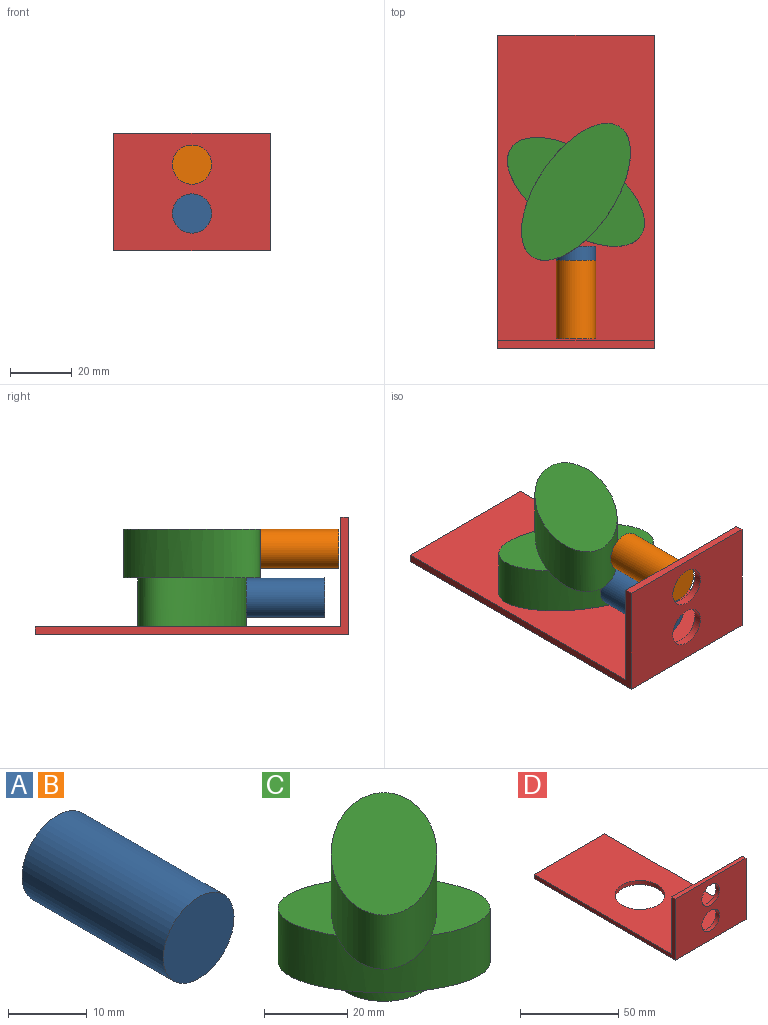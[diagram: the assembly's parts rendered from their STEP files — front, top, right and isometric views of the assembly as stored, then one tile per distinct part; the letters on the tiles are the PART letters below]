
ASSEMBLY  parts=4 mates=3
PART A: 3 faces, bbox 12.7x25.4x12.7 mm
  f0: cylinder r=6.35mm len=25.4mm, axis (0,1,0), area 1013.4mm2, adj f1,f2
  f1: plane 12.7x12.7mm, normal (0,-1,0), area 126.7mm2, adj f0
  f2: plane 12.7x12.7mm, normal (0,1,0), area 126.7mm2, adj f0
PART B: same geometry as A
PART C: 11 faces, bbox 40.2x40.2x34.3 mm
  f0: plane 29.06x29.06mm, normal (0,0,-1), area 253.4mm2, adj f2,f9
  f1: plane 20.08x20.08mm, normal (0,0,1), area 207.6mm2, adj f2,f7
  f2: extruded ~40.16x40.1mm, area 1953.4mm2, adj f0,f1,f3,f4,f5,f6
  f3: plane 20.08x20.08mm, normal (0,0,1), area 207.6mm2, adj f2,f7
  f4: plane 29.06x29.06mm, normal (0,0,-1), area 253.4mm2, adj f2,f9
  f5: plane 20.08x20.08mm, normal (0,0,-1), area 207.6mm2, adj f2,f7
  f6: plane 20.08x20.08mm, normal (0,0,-1), area 207.6mm2, adj f2,f7
  f7: extruded ~40.06x40.06mm, area 1953.4mm2, adj f1,f3,f5,f6,f8
  f8: plane 40.16x40.16mm, normal (0,0,1), area 1013.4mm2, adj f7
  f9: cylinder r=12.7mm len=25.4mm, axis (0,0,1), area 202.7mm2, adj f0,f4,f10
  f10: plane 25.4x25.4mm, normal (0,0,-1), area 506.7mm2, adj f9
PART D: 11 faces, bbox 50.8x101.6x38.1 mm
  f0: plane 99.06x50.8mm, normal (0,0,1), area 4525.5mm2, adj f1,f2,f3,f5,f10
  f1: plane 101.6x38.1mm, normal (1,0,0), area 348.4mm2, adj f0,f2,f4,f6,f7,f10
  f2: plane 50.8x2.54mm, normal (0,1,0), area 129mm2, adj f0,f1,f3,f6
  f3: plane 101.6x38.1mm, normal (-1,0,0), area 348.4mm2, adj f0,f2,f4,f6,f7,f10
  f4: plane 50.8x38.1mm, normal (0,-1,0), area 1682.1mm2, adj f1,f3,f6,f7,f8,f9
  f5: cylinder r=12.7mm len=25.4mm, axis (0,0,-1), area 202.7mm2, adj f0,f6
  f6: plane 101.6x50.8mm, normal (0,0,-1), area 4654.6mm2, adj f1,f2,f3,f4,f5
  f7: plane 50.8x2.54mm, normal (0,0,1), area 129mm2, adj f1,f3,f4,f10
  f8: cylinder r=6.35mm len=12.7mm, axis (0,-1,0), area 101.3mm2, adj f4,f10
  f9: cylinder r=6.35mm len=12.7mm, axis (0,-1,0), area 101.3mm2, adj f4,f10
  f10: plane 50.8x35.56mm, normal (0,1,0), area 1553.1mm2, adj f0,f1,f3,f7,f8,f9
PLACE A t=(0,-17.68,12.07)mm
PLACE B t=(0,-22.23,27.94)mm
PLACE C rot(axis=(0,0,1),11deg) t=(0,0,2.54)mm
PLACE D at identity fixed
MATE slider B.f0 <-> D.f8  axis (0,1,0) through (0,-34.93,27.94)mm
MATE slider A.f0 <-> D.f9  axis (0,1,0) through (0,-30.38,12.07)mm
MATE revolute D.f5 <-> C.f9  axis (0,0,-1) through (0,0,1.27)mm
